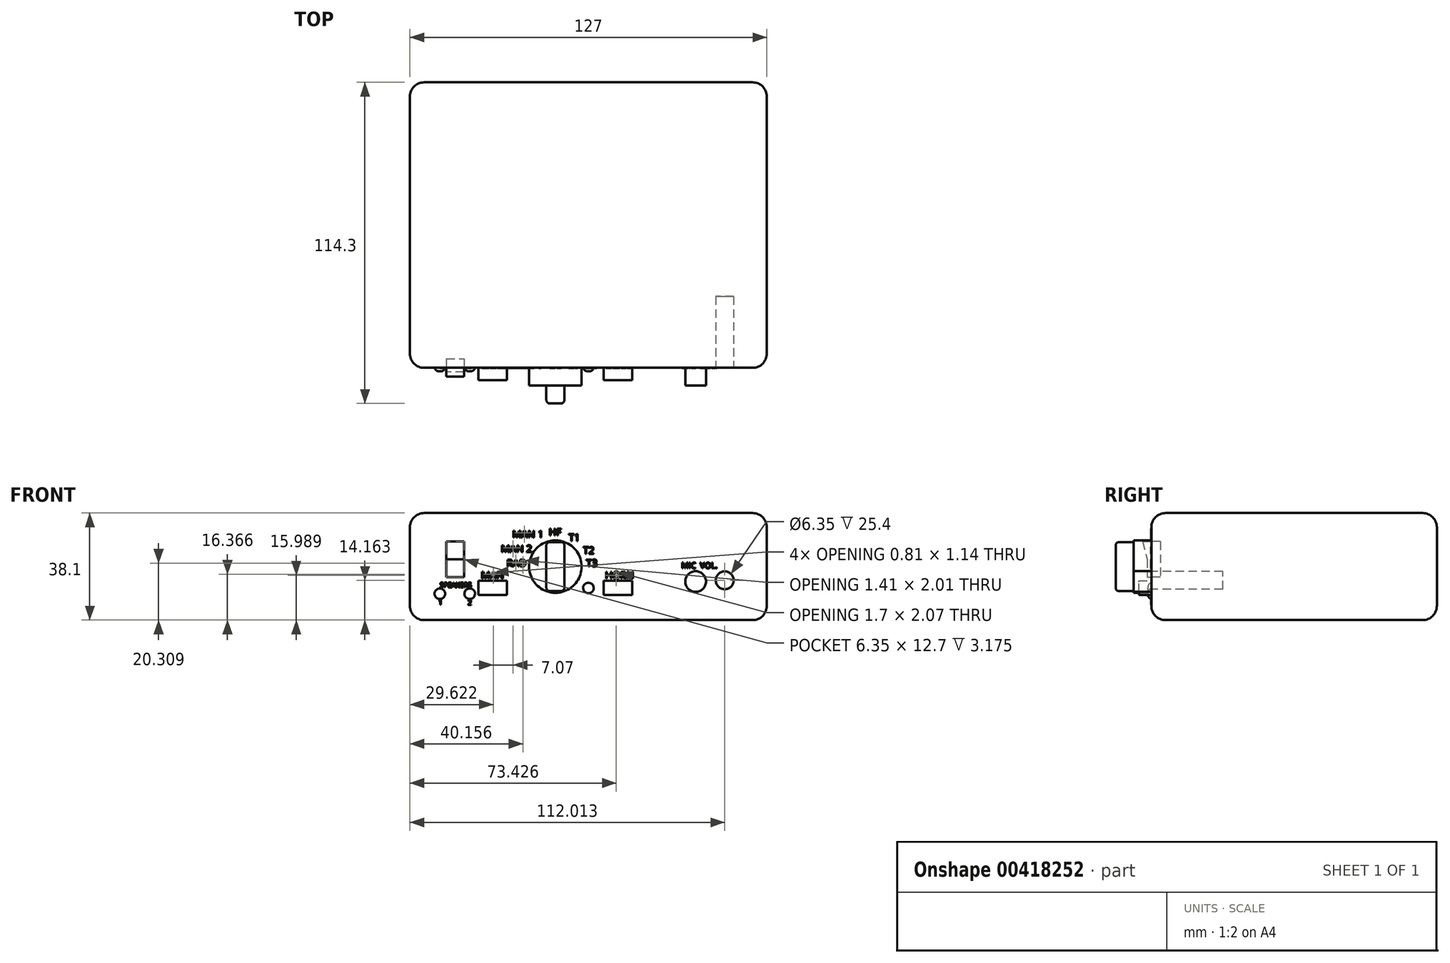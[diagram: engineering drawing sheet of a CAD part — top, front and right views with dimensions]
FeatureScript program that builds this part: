
annotation { "Feature Type Name" : "Feature", "Feature Type Description" : "" }
export const myFeature = defineFeature(function(context is Context, id is Id, definition is map)
    precondition{}
    {
        {
            var Q0;
            Q0=qCreatedBy(makeId("Front.planeOp"),FACE);
            var sketch = newSketch(context, id + "F0", { "sketchPlane" : qUnion([Q0])});
            skLineSegment(sketch, "E0.bottom", {"start": v(63.5, 19.05) * mm, "end": v(-63.5, 19.05) * mm});
            skLineSegment(sketch, "E0.top", {"start": v(63.5, -19.05) * mm, "end": v(-63.5, -19.05) * mm});
            skLineSegment(sketch, "E0.left", {"start": v(63.5, 19.05) * mm, "end": v(63.5, -19.05) * mm});
            skLineSegment(sketch, "E0.right", {"start": v(-63.5, 19.05) * mm, "end": v(-63.5, -19.05) * mm});
            skPoint(sketch, "E0.middle", {"position": v(0, 0) * mm});
            skSolve(sketch);
        }
        {
            var Q0;
            Q0=makeQuery(id+"F0.imprint","IMPRINT",FACE,{"disambiguationData":[TD([[makeQuery(id+"F0.imprint","IMPRINT",EDGE,{"derivedFrom":sQuery(id+"F0.wireOp",EDGE,"E0.bottom")}),1.0]])]});
            extrude(context, id + "F1", {"entities" : qUnion([Q0]), "oppositeDirection" : true, "depth" : 101.6 * mm});
        }
        {
            var Q0;
            Q0=makeQuery(id+"F1.opExtrude","SWEPT_FACE",FACE,{"disambiguationData":[OSD([sQuery(id+"F0.wireOp",EDGE,"E0.bottom")])]});
            var Q1;
            Q1=makeQuery(id+"F1.opExtrude","SWEPT_FACE",FACE,{"disambiguationData":[OSD([sQuery(id+"F0.wireOp",EDGE,"E0.right")])]});
            var Q2;
            Q2=makeQuery(id+"F1.opExtrude","SWEPT_FACE",FACE,{"disambiguationData":[OSD([sQuery(id+"F0.wireOp",EDGE,"E0.top")])]});
            var Q3;
            Q3=makeQuery(id+"F1.opExtrude","SWEPT_FACE",FACE,{"disambiguationData":[OSD([sQuery(id+"F0.wireOp",EDGE,"E0.left")])]});
            fillet(context, id + "F2", {"entities" : qUnion([Q0, Q1, Q2, Q3]), "radius" : 5.08 * mm, "tangentPropagation" : true, "allowEdgeOverflow" : false});
        }
        {
            var Q0;
            Q0=qCreatedBy(makeId("Front.planeOp"),FACE);
            var sketch = newSketch(context, id + "F3", { "sketchPlane" : qUnion([Q0])});
            skCircle(sketch, "E1", {"center": v(38.16, -5.32) * mm, "radius": 3.68 * mm});
            skSolve(sketch);
        }
        {
            var Q0;
            Q0=makeQuery(id+"F3.imprint","IMPRINT",FACE,{"disambiguationData":[TD([[makeQuery(id+"F3.imprint","IMPRINT",EDGE,{"derivedFrom":sQuery(id+"F3.wireOp",EDGE,"E1")}),1.0]])]});
            extrude(context, id + "F4", {"entities" : qUnion([Q0]), "operationType" : NewBodyOperationType.ADD, "depth" : 6.35 * mm});
        }
        {
            var Q0;
            Q0=qCreatedBy(makeId("Front.planeOp"),FACE);
            var sketch = newSketch(context, id + "F5", { "sketchPlane" : qUnion([Q0])});
            skCircle(sketch, "E2", {"center": v(48.51, -4.89) * mm, "radius": 3.18 * mm});
            skSolve(sketch);
        }
        {
            var Q0;
            Q0=makeQuery(id+"F5.imprint","IMPRINT",FACE,{"disambiguationData":[TD([[makeQuery(id+"F5.imprint","IMPRINT",EDGE,{"derivedFrom":sQuery(id+"F5.wireOp",EDGE,"E2")}),1.0]])]});
            extrude(context, id + "F6", {"entities" : qUnion([Q0]), "operationType" : NewBodyOperationType.REMOVE, "oppositeDirection" : true, "depth" : 25.4 * mm});
        }
        {
            var Q0;
            Q0=qCreatedBy(makeId("Front.planeOp"),FACE);
            var sketch = newSketch(context, id + "F7", { "sketchPlane" : qUnion([Q0])});
            skCircle(sketch, "E3", {"center": v(-11.76, 0) * mm, "radius": 9.33 * mm});
            skSolve(sketch);
        }
        {
            var Q0;
            Q0 = qSketchRegion(id + "F7", true);
            var Q1;
            Q1=makeQuery(id+"F7.imprint","IMPRINT",FACE,{"disambiguationData":[TD([[makeQuery(id+"F7.imprint","IMPRINT",EDGE,{"derivedFrom":sQuery(id+"F7.wireOp",EDGE,"E3")}),1.0]])]});
            extrude(context, id + "F8", {"entities" : qUnion([Q0, Q1]), "operationType" : NewBodyOperationType.ADD, "depth" : 6.35 * mm});
        }
        {
            var Q0;
            Q0=makeQuery(id+"F8.opExtrude","CAP_FACE",FACE,{"disambiguationData":[OSD([sQuery(id+"F7.wireOp",EDGE,"E3")])],"isStart":false});
            var sketch = newSketch(context, id + "F9", { "sketchPlane" : qUnion([Q0])});
            skLineSegment(sketch, "E4.bottom", {"start": v(-14.98, -8.75) * mm, "end": v(-8.54, -8.75) * mm});
            skLineSegment(sketch, "E4.top", {"start": v(-14.98, 8.75) * mm, "end": v(-8.54, 8.75) * mm});
            skLineSegment(sketch, "E4.left", {"start": v(-14.98, -8.75) * mm, "end": v(-14.98, 8.75) * mm});
            skLineSegment(sketch, "E4.right", {"start": v(-8.54, -8.75) * mm, "end": v(-8.54, 8.75) * mm});
            skPoint(sketch, "E4.middle", {"position": v(-11.76, 0) * mm});
            skSolve(sketch);
        }
        {
            var Q0;
            Q0=makeQuery(id+"F9.imprint","IMPRINT",FACE,{"disambiguationData":[TD([[makeQuery(id+"F9.imprint","IMPRINT",EDGE,{"derivedFrom":sQuery(id+"F9.wireOp",EDGE,"E4.bottom")}),1.0]])]});
            extrude(context, id + "F10", {"entities" : qUnion([Q0]), "operationType" : NewBodyOperationType.ADD, "depth" : 6.35 * mm});
        }
        {
            var Q0;
            Q0=makeQuery(id+"F10.opExtrude","SWEPT_EDGE",EDGE,{"disambiguationData":[OSD([sQuery(id+"F7.wireOp",EDGE,"E3"),sQuery(id+"F9.wireOp",EDGE,"E4.top"),sQuery(id+"F9.wireOp",EDGE,"E4.left")])]});
            var Q1;
            Q1=makeQuery(id+"F10.opExtrude","SWEPT_EDGE",EDGE,{"disambiguationData":[OSD([sQuery(id+"F7.wireOp",EDGE,"E3"),sQuery(id+"F9.wireOp",EDGE,"E4.bottom"),sQuery(id+"F9.wireOp",EDGE,"E4.left")])]});
            var Q2;
            Q2=makeQuery(id+"F10.opExtrude","SWEPT_EDGE",EDGE,{"disambiguationData":[OSD([sQuery(id+"F7.wireOp",EDGE,"E3"),sQuery(id+"F9.wireOp",EDGE,"E4.top"),sQuery(id+"F9.wireOp",EDGE,"E4.right")])]});
            var Q3;
            Q3=makeQuery(id+"F10.opExtrude","SWEPT_EDGE",EDGE,{"disambiguationData":[OSD([sQuery(id+"F7.wireOp",EDGE,"E3"),sQuery(id+"F9.wireOp",EDGE,"E4.bottom"),sQuery(id+"F9.wireOp",EDGE,"E4.right")])]});
            var Q4;
            Q4=makeQuery(id+"F10.opExtrude","CAP_EDGE",EDGE,{"disambiguationData":[OSD([sQuery(id+"F9.wireOp",EDGE,"E4.right")])],"isStart":false});
            var Q5;
            Q5=makeQuery(id+"F10.opExtrude","CAP_EDGE",EDGE,{"disambiguationData":[OSD([sQuery(id+"F9.wireOp",EDGE,"E4.top")])],"isStart":false});
            var Q6;
            Q6=makeQuery(id+"F10.opExtrude","CAP_EDGE",EDGE,{"disambiguationData":[OSD([sQuery(id+"F9.wireOp",EDGE,"E4.left")])],"isStart":false});
            var Q7;
            Q7=makeQuery(id+"F10.opExtrude","CAP_EDGE",EDGE,{"disambiguationData":[OSD([sQuery(id+"F9.wireOp",EDGE,"E4.bottom")])],"isStart":false});
            fillet(context, id + "F11", {"entities" : qUnion([Q0, Q1, Q2, Q3, Q4, Q5, Q6, Q7]), "radius" : 1.27 * mm, "tangentPropagation" : true, "allowEdgeOverflow" : false});
        }
        {
            var Q0;
            Q0=qCreatedBy(makeId("Front.planeOp"),FACE);
            var sketch = newSketch(context, id + "F12", { "sketchPlane" : qUnion([Q0])});
            skLineSegment(sketch, "E5.bottom", {"start": v(15.59, -10.16) * mm, "end": v(5.43, -10.16) * mm});
            skLineSegment(sketch, "E5.top", {"start": v(15.59, -5.08) * mm, "end": v(5.43, -5.08) * mm});
            skLineSegment(sketch, "E5.left", {"start": v(15.59, -10.16) * mm, "end": v(15.59, -5.08) * mm});
            skLineSegment(sketch, "E5.right", {"start": v(5.43, -10.16) * mm, "end": v(5.43, -5.08) * mm});
            skPoint(sketch, "E5.middle", {"position": v(10.5, -7.62) * mm});
            skLineSegment(sketch, "E6.bottom", {"start": v(-28.95, -10.16) * mm, "end": v(-39.11, -10.16) * mm});
            skLineSegment(sketch, "E6.top", {"start": v(-28.95, -5.08) * mm, "end": v(-39.11, -5.08) * mm});
            skLineSegment(sketch, "E6.left", {"start": v(-28.95, -10.16) * mm, "end": v(-28.95, -5.08) * mm});
            skLineSegment(sketch, "E6.right", {"start": v(-39.11, -10.16) * mm, "end": v(-39.11, -5.08) * mm});
            skPoint(sketch, "E6.middle", {"position": v(-34.03, -7.62) * mm});
            skCircle(sketch, "E7", {"center": v(0, -7.62) * mm, "radius": 1.9 * mm});
            skSolve(sketch);
        }
        {
            var Q0;
            Q0=makeQuery(id+"F12.imprint","IMPRINT",FACE,{"disambiguationData":[TD([[makeQuery(id+"F12.imprint","IMPRINT",EDGE,{"derivedFrom":sQuery(id+"F12.wireOp",EDGE,"E5.bottom")}),-1.0]])]});
            var Q1;
            Q1=makeQuery(id+"F12.imprint","IMPRINT",FACE,{"disambiguationData":[TD([[makeQuery(id+"F12.imprint","IMPRINT",EDGE,{"derivedFrom":sQuery(id+"F12.wireOp",EDGE,"E6.bottom")}),-1.0]])]});
            extrude(context, id + "F13", {"entities" : qUnion([Q0, Q1]), "operationType" : NewBodyOperationType.ADD, "depth" : 4.44 * mm});
        }
        {
            var Q0;
            Q0=qCreatedBy(makeId("Front.planeOp"),FACE);
            var sketch = newSketch(context, id + "F14", { "sketchPlane" : qUnion([Q0])});
            skText(sketch, "E8", { "text": "MAN", "fontName": "OpenSans-Regular.ttf"});
            skText(sketch, "E9", { "text": "HORN", "fontName": "OpenSans-Regular.ttf"});
            skText(sketch, "E10", { "text": "MIC  VOL.", "fontName": "OpenSans-Regular.ttf"});
            skText(sketch, "E11", { "text": "HF", "fontName": "OpenSans-Regular.ttf"});
            skText(sketch, "E12", { "text": "RAD", "fontName": "OpenSans-Regular.ttf"});
            skText(sketch, "E13", { "text": "MAN 2", "fontName": "OpenSans-Regular.ttf"});
            skText(sketch, "E14", { "text": "MAN 1", "fontName": "OpenSans-Regular.ttf"});
            skText(sketch, "E15", { "text": "T3", "fontName": "OpenSans-Regular.ttf"});
            skText(sketch, "E16", { "text": "T1", "fontName": "OpenSans-Regular.ttf"});
            skText(sketch, "E17", { "text": "T2", "fontName": "OpenSans-Regular.ttf"});
            const initialGuessF14  = {"E8": [-0.03818, -0.00432, 1, 0, 0.00254], "E9": [0.00595, -0.00432, 1, 0, 0.00254], "E10": [0.03312, -0.00063, 1, 0, 0.00204], "E11": [-0.01405, 0.01106, 1, 0, 0.00254], "E12": [-0.0291, 0, 1, 0, 0.00254], "E13": [-0.03111, 0.00508, 1, 0, 0.00254], "E14": [-0.02706, 0.0103, 1, 0, 0.00254], "E15": [-0.00077, 0, 1, 0, 0.00254], "E16": [-0.00702, 0.00905, 1, 0, 0.00254], "E17": [-0.00188, 0.00448, 1, 0, 0.00254]};
            skSetInitialGuess(sketch, initialGuessF14);
            skSolve(sketch);
        }
        {
            var Q0;
            Q0=makeQuery(id+"F1.opExtrude","CAP_FACE",FACE,{"disambiguationData":[OSD([sQuery(id+"F0.wireOp",EDGE,"E0.bottom"),sQuery(id+"F0.wireOp",EDGE,"E0.top"),sQuery(id+"F0.wireOp",EDGE,"E0.left"),sQuery(id+"F0.wireOp",EDGE,"E0.right")])],"isStart":true});
            var sketch = newSketch(context, id + "F15", { "sketchPlane" : qUnion([Q0])});
            skLineSegment(sketch, "E18.bottom", {"start": v(-51.85, 10.16) * mm, "end": v(-42.96, 10.16) * mm});
            skLineSegment(sketch, "E18.top", {"start": v(-51.85, -5.08) * mm, "end": v(-42.96, -5.08) * mm});
            skLineSegment(sketch, "E18.left", {"start": v(-51.85, 10.16) * mm, "end": v(-51.85, -5.08) * mm});
            skLineSegment(sketch, "E18.right", {"start": v(-42.96, 10.16) * mm, "end": v(-42.96, -5.08) * mm});
            skSolve(sketch);
        }
        {
            var Q0;
            Q0=qCreatedBy(makeId("Front.planeOp"),FACE);
            var sketch = newSketch(context, id + "F16", { "sketchPlane" : qUnion([Q0])});
            skCircle(sketch, "E19", {"center": v(-52.86, -9.65) * mm, "radius": 1.9 * mm});
            skCircle(sketch, "E20", {"center": v(-42.24, -9.65) * mm, "radius": 1.9 * mm});
            skText(sketch, "E21", { "text": "SPEAKERS\n", "fontName": "OpenSans-Regular.ttf"});
            skText(sketch, "E22", { "text": "2", "fontName": "OpenSans-Regular.ttf"});
            skText(sketch, "E23", { "text": "1", "fontName": "OpenSans-Regular.ttf"});
            const initialGuessF16  = {"E21": [-0.05283, -0.00739, 1, 0, 0.00173], "E22": [-0.04297, -0.01367, 1, 0, 0.0018], "E23": [-0.05338, -0.01356, 1, 0, 0.0018]};
            skSetInitialGuess(sketch, initialGuessF16);
            skSolve(sketch);
        }
        {
            var Q0;
            Q0=makeQuery(id+"F16.imprint","IMPRINT",FACE,{"disambiguationData":[TD([[makeQuery(id+"F16.imprint","IMPRINT",EDGE,{"derivedFrom":sQuery(id+"F16.wireOp",EDGE,"E20")}),1.0]])]});
            var Q1;
            Q1=makeQuery(id+"F16.imprint","IMPRINT",FACE,{"disambiguationData":[TD([[makeQuery(id+"F16.imprint","IMPRINT",EDGE,{"derivedFrom":sQuery(id+"F16.wireOp",EDGE,"E19")}),1.0]])]});
            var Q2;
            Q2=makeQuery(id+"F12.imprint","IMPRINT",FACE,{"disambiguationData":[TD([[makeQuery(id+"F12.imprint","IMPRINT",EDGE,{"derivedFrom":sQuery(id+"F12.wireOp",EDGE,"E7")}),1.0]])]});
            extrude(context, id + "F17", {"entities" : qUnion([Q0, Q1, Q2]), "depth" : 1.27 * mm});
        }
        {
            var Q0;
            Q0=makeQuery(id+"F15.imprint","IMPRINT",FACE,{"disambiguationData":[TD([[makeQuery(id+"F15.imprint","IMPRINT",EDGE,{"derivedFrom":sQuery(id+"F15.wireOp",EDGE,"E18.bottom")}),-1.0]])]});
            var sketch = newSketch(context, id + "F18", { "sketchPlane" : qUnion([Q0])});
            skLineSegment(sketch, "E24.bottom", {"start": v(-50.58, 8.89) * mm, "end": v(-44.23, 8.89) * mm});
            skLineSegment(sketch, "E24.top", {"start": v(-50.58, -3.81) * mm, "end": v(-44.23, -3.81) * mm});
            skLineSegment(sketch, "E24.left", {"start": v(-50.58, 8.89) * mm, "end": v(-50.58, -3.81) * mm});
            skLineSegment(sketch, "E24.right", {"start": v(-44.23, 8.89) * mm, "end": v(-44.23, -3.81) * mm});
            skSolve(sketch);
        }
        {
            var Q0;
            Q0=makeQuery(id+"F18.imprint","IMPRINT",FACE,{"disambiguationData":[TD([[makeQuery(id+"F18.imprint","IMPRINT",EDGE,{"derivedFrom":sQuery(id+"F18.wireOp",EDGE,"E24.bottom")}),-1.0]])]});
            extrude(context, id + "F19", {"entities" : qUnion([Q0]), "operationType" : NewBodyOperationType.REMOVE, "oppositeDirection" : true, "depth" : 3.17 * mm});
        }
        {
            var Q0;
            Q0 = qSketchRegion(id + "F18", true);
            extrude(context, id + "F20", {"entities" : qUnion([Q0]), "depth" : 3.17 * mm});
        }
        {
            var Q0;
            Q0=makeQuery(id+"F20.opExtrude","SWEPT_FACE",FACE,{"disambiguationData":[OSD([sQuery(id+"F18.wireOp",EDGE,"E24.left")])]});
            var sketch = newSketch(context, id + "F21", { "sketchPlane" : qUnion([Q0])});
            skLineSegment(sketch, "E25", {"start": v(3.18, 8.89) * mm, "end": v(1.5, 2.54) * mm});
            skPoint(sketch, "E25.endSnap0", {"position": v(0, 2.54) * mm});
            skLineSegment(sketch, "E26", {"start": v(1.5, 2.54) * mm, "end": v(1.5, -3.81) * mm});
            skPoint(sketch, "E26.endSnap0", {"position": v(1.59, -3.81) * mm});
            skSolve(sketch);
        }
        {
            var Q0;
            Q0=makeQuery(id+"F21.imprint","IMPRINT",FACE,{"disambiguationData":[TD([[makeQuery(id+"F21.imprint","IMPRINT",EDGE,{"derivedFrom":sQuery(id+"F21.wireOp",EDGE,"E25")}),1.0]])]});
            var Q1;
            Q1=makeQuery(id+"F20.opExtrude","SWEPT_FACE",FACE,{"disambiguationData":[OSD([sQuery(id+"F18.wireOp",EDGE,"E24.right")])]});
            extrude(context, id + "F22", {"entities" : qUnion([Q0]), "operationType" : NewBodyOperationType.REMOVE, "endBound" : BoundingType.UP_TO_SURFACE, "oppositeDirection" : true, "endBoundEntityFace" : qUnion([Q1]), "depth" : 25.4 * mm});
        }
        {
            var Q0;
            Q0=makeQuery(id+"F17.opExtrude","CAP_EDGE",EDGE,{"disambiguationData":[OSD([sQuery(id+"F16.wireOp",EDGE,"E19")])],"isStart":false});
            var Q1;
            Q1=makeQuery(id+"F17.opExtrude","CAP_EDGE",EDGE,{"disambiguationData":[OSD([sQuery(id+"F16.wireOp",EDGE,"E20")])],"isStart":false});
            var Q2;
            Q2=makeQuery(id+"F17.opExtrude","CAP_EDGE",EDGE,{"disambiguationData":[OSD([sQuery(id+"F12.wireOp",EDGE,"E7")])],"isStart":false});
            fillet(context, id + "F23", {"entities" : qUnion([Q0, Q1, Q2]), "radius" : 1.9 * mm, "tangentPropagation" : true, "rho" : 0.5, "crossSection" : FilletCrossSection.CONIC, "allowEdgeOverflow" : false});
        }
        {
            var Q0;
            Q0 = qSketchRegion(id + "F14", true);
            extrude(context, id + "F24", {"entities" : qUnion([Q0]), "depth" : 0.03 * mm});
        }
        {
            var Q0;
            Q0=makeQuery(id+"F16.imprint","IMPRINT",FACE,{"disambiguationData":[TD([[makeQuery(id+"F16.imprint","IMPRINT",EDGE,{"derivedFrom":sQuery(id+"F16.wireOp",EDGE,"E22.sketch_text.stroke-0")}),-1.0]])]});
            var Q1;
            Q1=makeQuery(id+"F16.imprint","IMPRINT",FACE,{"disambiguationData":[TD([[makeQuery(id+"F16.imprint","IMPRINT",EDGE,{"derivedFrom":sQuery(id+"F16.wireOp",EDGE,"E23.sketch_text.stroke-0")}),-1.0]])]});
            extrude(context, id + "F25", {"entities" : qUnion([Q0, Q1]), "depth" : 0.03 * mm});
        }
        {
            var Q0;
            Q0=makeQuery(id+"F16.imprint","IMPRINT",FACE,{"disambiguationData":[TD([[makeQuery(id+"F16.imprint","IMPRINT",EDGE,{"derivedFrom":sQuery(id+"F16.wireOp",EDGE,"E21.sketch_text.stroke-77")}),-1.0]])]});
            var Q1;
            Q1=makeQuery(id+"F16.imprint","IMPRINT",FACE,{"disambiguationData":[TD([[makeQuery(id+"F16.imprint","IMPRINT",EDGE,{"derivedFrom":sQuery(id+"F16.wireOp",EDGE,"E21.sketch_text.stroke-107")}),-1.0]])]});
            var Q2;
            Q2=makeQuery(id+"F16.imprint","IMPRINT",FACE,{"disambiguationData":[TD([[makeQuery(id+"F16.imprint","IMPRINT",EDGE,{"derivedFrom":sQuery(id+"F16.wireOp",EDGE,"E21.sketch_text.stroke-0")}),-1.0]])]});
            var Q3;
            Q3=makeQuery(id+"F16.imprint","IMPRINT",FACE,{"disambiguationData":[TD([[makeQuery(id+"F16.imprint","IMPRINT",EDGE,{"derivedFrom":sQuery(id+"F16.wireOp",EDGE,"E21.sketch_text.stroke-52")}),-1.0]])]});
            var Q4;
            Q4=makeQuery(id+"F16.imprint","IMPRINT",FACE,{"disambiguationData":[TD([[makeQuery(id+"F16.imprint","IMPRINT",EDGE,{"derivedFrom":sQuery(id+"F16.wireOp",EDGE,"E21.sketch_text.stroke-25")}),-1.0]])]});
            var Q5;
            Q5=makeQuery(id+"F16.imprint","IMPRINT",FACE,{"disambiguationData":[TD([[makeQuery(id+"F16.imprint","IMPRINT",EDGE,{"derivedFrom":sQuery(id+"F16.wireOp",EDGE,"E21.sketch_text.stroke-60")}),1.0]])]});
            var Q6;
            Q6=makeQuery(id+"F16.imprint","IMPRINT",FACE,{"disambiguationData":[TD([[makeQuery(id+"F16.imprint","IMPRINT",EDGE,{"derivedFrom":sQuery(id+"F16.wireOp",EDGE,"E21.sketch_text.stroke-33")}),1.0]])]});
            var Q7;
            Q7=makeQuery(id+"F16.imprint","IMPRINT",FACE,{"disambiguationData":[TD([[makeQuery(id+"F16.imprint","IMPRINT",EDGE,{"derivedFrom":sQuery(id+"F16.wireOp",EDGE,"E21.sketch_text.stroke-89")}),-1.0]])]});
            var Q8;
            Q8=makeQuery(id+"F16.imprint","IMPRINT",FACE,{"disambiguationData":[TD([[makeQuery(id+"F16.imprint","IMPRINT",EDGE,{"derivedFrom":sQuery(id+"F16.wireOp",EDGE,"E21.sketch_text.stroke-100")}),1.0]])]});
            var Q9;
            Q9=makeQuery(id+"F16.imprint","IMPRINT",FACE,{"disambiguationData":[TD([[makeQuery(id+"F16.imprint","IMPRINT",EDGE,{"derivedFrom":sQuery(id+"F16.wireOp",EDGE,"E21.sketch_text.stroke-40")}),-1.0]])]});
            var Q10;
            Q10=makeQuery(id+"F16.imprint","IMPRINT",FACE,{"disambiguationData":[TD([[makeQuery(id+"F16.imprint","IMPRINT",EDGE,{"derivedFrom":sQuery(id+"F16.wireOp",EDGE,"E21.sketch_text.stroke-65")}),-1.0]])]});
            extrude(context, id + "F26", {"entities" : qUnion([Q0, Q1, Q2, Q3, Q4, Q5, Q6, Q7, Q8, Q9, Q10]), "depth" : 0.03 * mm});
        }
    });
